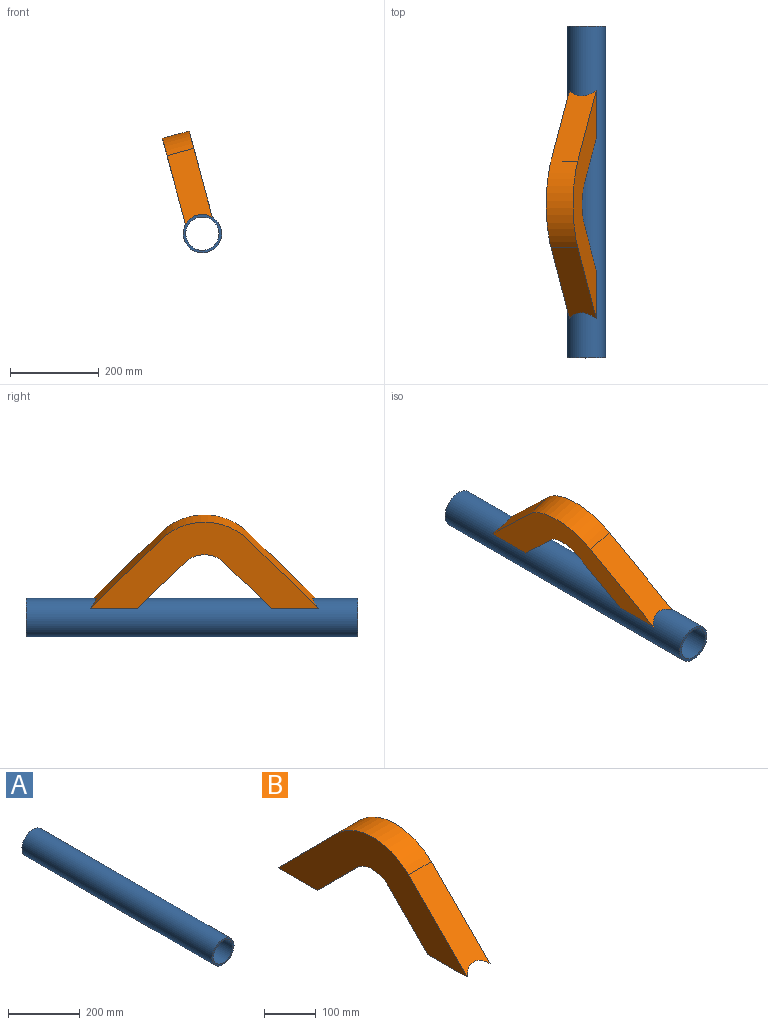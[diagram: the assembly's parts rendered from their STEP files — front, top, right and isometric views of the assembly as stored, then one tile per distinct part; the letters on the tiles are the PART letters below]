
ASSEMBLY  parts=2 mates=1
PART A: 4 faces, bbox 86.9x750x86.9 mm
  f0: cylinder r=37.61mm len=750mm, axis (0,1,0), area 177219mm2, adj f2,f3
  f1: cylinder r=43.47mm len=750mm, axis (0,1,0), area 204839.3mm2, adj f2,f3
  f2: plane 86.94x86.94mm, normal (0,-1,0), area 1492.9mm2, adj f0,f1
  f3: plane 86.94x86.94mm, normal (0,1,0), area 1492.9mm2, adj f0,f1
PART B: 18 faces, bbox 62.7x516.5x201.8 mm
  f0: plane 516.45x201.82mm, normal (1,0,0), area 40819.4mm2, adj f2,f3,f4,f5,f6,f7,f8,f9
  f1: plane 516.45x201.82mm, normal (-1,0,0), area 40819.4mm2, adj f2,f3,f4,f5,f6,f7,f8,f9
  f2: plane 107.49x106.98mm, normal (0,0.71,-0.71), area 8696.4mm2, adj f0,f1,f4,f9
  f3: plane 161.15x160.39mm, normal (0,-0.71,0.71), area 13445.9mm2, adj f0,f1,f5,f9
  f4: cylinder r=61.96mm len=87.84mm, axis (-1,0,0), area 6124.3mm2, adj f0,f1,f2,f6
  f5: cylinder r=138.04mm len=195.68mm, axis (-1,0,0), area 13643.4mm2, adj f0,f1,f3,f7
  f6: plane 107.49x106.98mm, normal (0,-0.71,-0.71), area 8696.4mm2, adj f0,f1,f4,f8
  f7: plane 161.15x160.39mm, normal (0,0.71,0.71), area 13445.9mm2, adj f0,f1,f5,f8
  f8: cylinder r=43.47mm len=120.68mm, axis (0,1,0), area 1835.5mm2, adj f0,f1,f6,f7,f12,f13,f14,f16
  f9: cylinder r=43.47mm len=120.68mm, axis (0,1,0), area 1835.5mm2, adj f0,f1,f2,f3,f14,f15,f16,f17
  f10: cylinder r=65.96mm len=93.51mm, axis (-1,0,0), area 5688.2mm2, adj f13,f14,f16,f17
  f11: cylinder r=134.04mm len=190.01mm, axis (-1,0,0), area 11558.6mm2, adj f12,f14,f15,f16
  f12: plane 154.65x153.92mm, normal (0,-0.71,-0.71), area 11430.7mm2, adj f8,f11,f14,f16
  f13: plane 106.63x106.13mm, normal (0,0.71,0.71), area 7722.7mm2, adj f8,f10,f14,f16
  f14: plane 497.84x194.14mm, normal (1,0,0), area 35820.3mm2, adj f8,f9,f10,f11,f12,f13,f15,f17
  f15: plane 154.65x153.92mm, normal (0,0.71,-0.71), area 11430.7mm2, adj f9,f11,f14,f16
  f16: plane 497.84x194.14mm, normal (-1,0,0), area 35820.3mm2, adj f8,f9,f10,f11,f12,f13,f15,f17
  f17: plane 106.63x106.13mm, normal (0,-0.71,0.71), area 7722.7mm2, adj f9,f10,f14,f16
PLACE A at identity fixed
PLACE B rot(axis=(0,-1,0),15deg) t=(0,-28.15,0)mm
MATE cylindrical B.f8 <-> A.f0  axis (0,1,0) through (0,-28.15,0)mm
